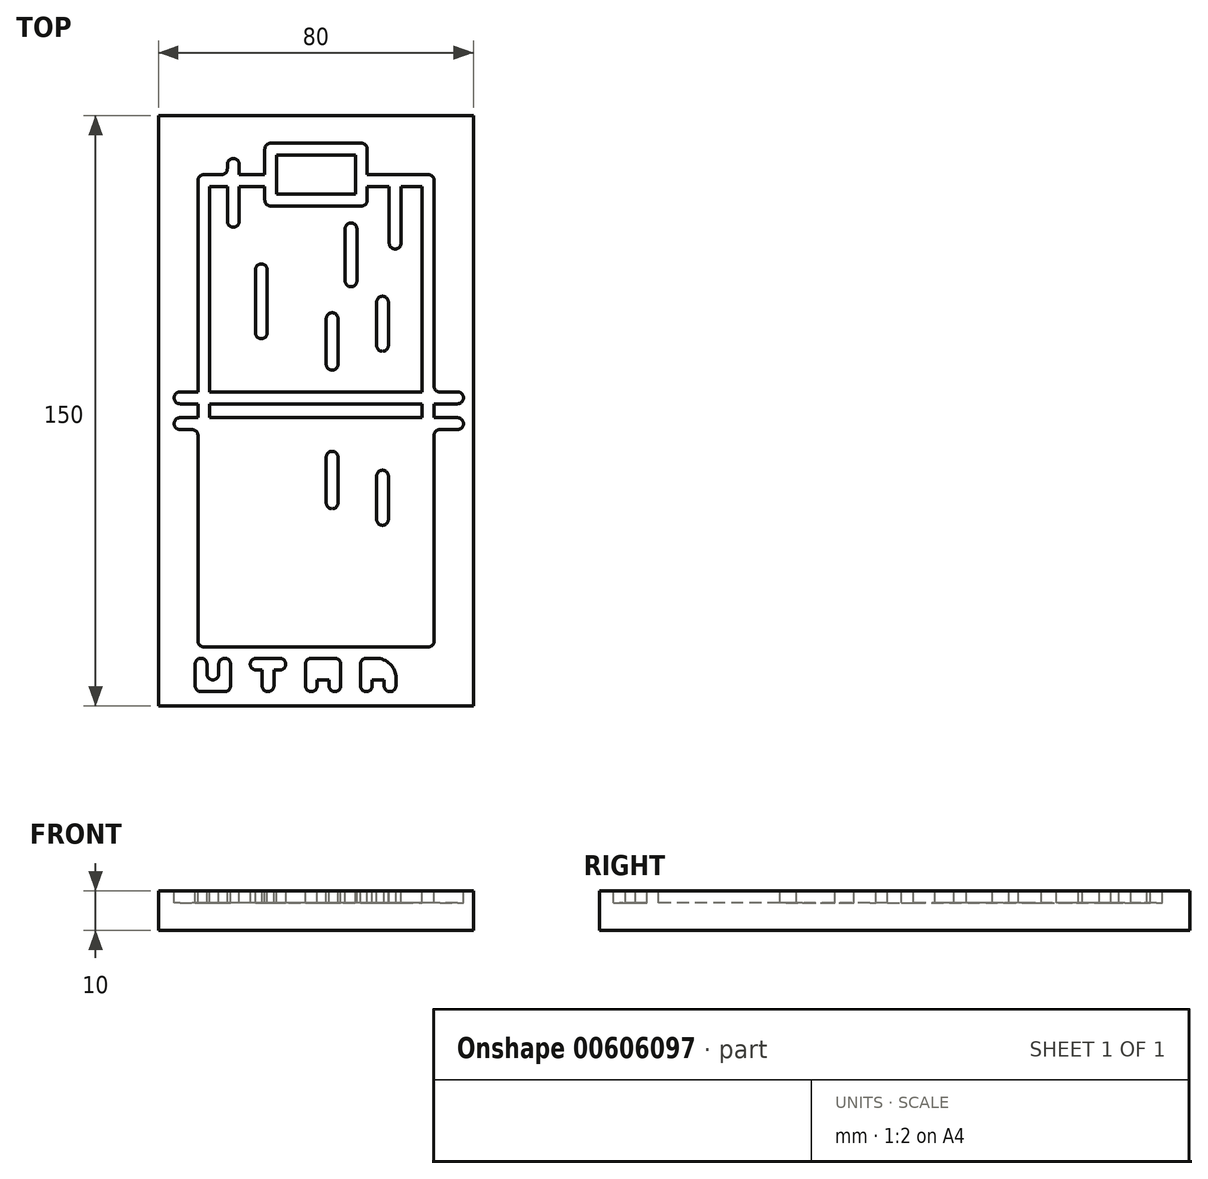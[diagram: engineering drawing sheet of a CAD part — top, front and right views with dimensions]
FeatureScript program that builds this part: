
annotation { "Feature Type Name" : "Feature", "Feature Type Description" : "" }
export const myFeature = defineFeature(function(context is Context, id is Id, definition is map)
    precondition{}
    {
        {
            var Q0;
            Q0=qCreatedBy(makeId("Top.planeOp"),FACE);
            var sketch = newSketch(context, id + "F0", { "sketchPlane" : qUnion([Q0])});
            skLineSegment(sketch, "E0.bottom", {"start": v(40, 75) * mm, "end": v(-40, 75) * mm});
            skLineSegment(sketch, "E0.top", {"start": v(40, -75) * mm, "end": v(-40, -75) * mm});
            skLineSegment(sketch, "E0.left", {"start": v(40, 75) * mm, "end": v(40, -75) * mm});
            skLineSegment(sketch, "E0.right", {"start": v(-40, 75) * mm, "end": v(-40, -75) * mm});
            skPoint(sketch, "E0.middle", {"position": v(0, 0) * mm});
            skSolve(sketch);
        }
        {
            var Q0;
            Q0 = qSketchRegion(id + "F0", true);
            extrude(context, id + "F1", {"entities" : qUnion([Q0]), "depth" : 10 * mm, "offsetDistance" : 25.4 * mm});
        }
        {
            var Q0;
            Q0=makeQuery(id+"F1.opExtrude","CAP_FACE",FACE,{"disambiguationData":[OSD([sQuery(id+"F0.wireOp",EDGE,"E0.bottom"),sQuery(id+"F0.wireOp",EDGE,"E0.top"),sQuery(id+"F0.wireOp",EDGE,"E0.left"),sQuery(id+"F0.wireOp",EDGE,"E0.right")])],"isStart":false});
            var sketch = newSketch(context, id + "F2", { "sketchPlane" : qUnion([Q0])});
            skLineSegment(sketch, "E1.bottom", {"start": v(30, 60) * mm, "end": v(13, 60) * mm});
            skLineSegment(sketch, "E1.top", {"start": v(30, -60) * mm, "end": v(-30, -60) * mm});
            skLineSegment(sketch, "E1.left", {"start": v(30, 60) * mm, "end": v(30, 4.77) * mm});
            skLineSegment(sketch, "E1.right", {"start": v(-30, 60) * mm, "end": v(-30, 4.77) * mm});
            skPoint(sketch, "E1.middle", {"position": v(0, 0) * mm});
            skLineSegment(sketch, "E2", {"start": v(-15.4, 35.8) * mm, "end": v(-15.4, 19.8) * mm});
            skLineSegment(sketch, "E3.bottom", {"start": v(10, 55) * mm, "end": v(-10, 55) * mm});
            skLineSegment(sketch, "E3.top", {"start": v(10, 65) * mm, "end": v(-10, 65) * mm});
            skLineSegment(sketch, "E3.left", {"start": v(10, 55) * mm, "end": v(10, 65) * mm});
            skLineSegment(sketch, "E3.right", {"start": v(-10, 55) * mm, "end": v(-10, 65) * mm});
            skPoint(sketch, "E3.middle", {"position": v(0, 60) * mm});
            skLineSegment(sketch, "E4", {"start": v(7.4, 46.2) * mm, "end": v(7.4, 33) * mm});
            skLineSegment(sketch, "E5", {"start": v(2.6, 23.4) * mm, "end": v(2.6, 11.8) * mm});
            skLineSegment(sketch, "E6", {"start": v(18.6, 57) * mm, "end": v(18.6, 42.6) * mm});
            skLineSegment(sketch, "E7", {"start": v(15.4, 27.6) * mm, "end": v(15.4, 16.6) * mm});
            skLineSegment(sketch, "E8", {"start": v(-34.55, 4.77) * mm, "end": v(-30, 4.77) * mm});
            skLineSegment(sketch, "E9", {"start": v(35.96, 1.77) * mm, "end": v(30, 1.77) * mm});
            skLineSegment(sketch, "E10", {"start": v(-30, -60) * mm, "end": v(-27, -60) * mm});
            skLineSegment(sketch, "E11", {"start": v(-27, -57) * mm, "end": v(-27, -4.77) * mm});
            skLineSegment(sketch, "E12", {"start": v(-30, 60) * mm, "end": v(-30, 57) * mm});
            skLineSegment(sketch, "E13", {"start": v(-27, 57) * mm, "end": v(-22.51, 57) * mm});
            skLineSegment(sketch, "E14", {"start": v(30, 60) * mm, "end": v(27, 60) * mm});
            skLineSegment(sketch, "E15", {"start": v(27, -57) * mm, "end": v(27, -4.77) * mm});
            skLineSegment(sketch, "E16", {"start": v(30, -60) * mm, "end": v(30, -57) * mm});
            skLineSegment(sketch, "E17", {"start": v(27, -57) * mm, "end": v(13.35, -57) * mm});
            skPoint(sketch, "E18.orphan", {"position": v(27, -60) * mm});
            skArc(sketch, "E19", {"start": v(-34.55, 1.77) * mm, "mid": v(-36.05, 3.27) * mm, "end": v(-34.55, 4.77) * mm});
            skArc(sketch, "E20", {"start": v(35.96, 1.77) * mm, "mid": v(37.46, 3.27) * mm, "end": v(35.96, 4.77) * mm});
            skArc(sketch, "E21.MirrorCS", {"start": v(35.96, -1.77) * mm, "mid": v(37.46, -3.27) * mm, "end": v(35.96, -4.77) * mm});
            skArc(sketch, "E22.MirrorCS", {"start": v(-34.55, -1.77) * mm, "mid": v(-36.05, -3.27) * mm, "end": v(-34.55, -4.77) * mm});
            skLineSegment(sketch, "E23.MirrorCS", {"start": v(35.96, -1.77) * mm, "end": v(30, -1.77) * mm});
            skLineSegment(sketch, "E24.MirrorCS", {"start": v(-34.55, -4.77) * mm, "end": v(-30, -4.77) * mm});
            skLineSegment(sketch, "E25", {"start": v(13, 65) * mm, "end": v(13, 60) * mm});
            skLineSegment(sketch, "E26", {"start": v(13, 52) * mm, "end": v(-13, 52) * mm});
            skLineSegment(sketch, "E27", {"start": v(-13, 52) * mm, "end": v(-13, 57) * mm});
            skLineSegment(sketch, "E28", {"start": v(-13, 68) * mm, "end": v(13, 68) * mm});
            skLineSegment(sketch, "E29", {"start": v(13, 68) * mm, "end": v(13, 65) * mm});
            skLineSegment(sketch, "E30.trimOffspring", {"start": v(-27, 4.77) * mm, "end": v(-27, 57) * mm});
            skLineSegment(sketch, "E31.trimOffspring", {"start": v(-27, 4.77) * mm, "end": v(27, 4.77) * mm});
            skLineSegment(sketch, "E32.trimOffspring", {"start": v(-30, 1.77) * mm, "end": v(-30, -1.77) * mm});
            skLineSegment(sketch, "E33.trimOffspring", {"start": v(-30, 1.77) * mm, "end": v(-34.55, 1.77) * mm});
            skLineSegment(sketch, "E34.trimOffspring", {"start": v(-30, -1.77) * mm, "end": v(-34.55, -1.77) * mm});
            skLineSegment(sketch, "E35.trimOffspring", {"start": v(-30, -4.77) * mm, "end": v(-30, -60) * mm});
            skLineSegment(sketch, "E36.trimOffspring", {"start": v(-27, -4.77) * mm, "end": v(27, -4.77) * mm});
            skLineSegment(sketch, "E37.trimOffspring", {"start": v(-27, -1.77) * mm, "end": v(-27, 1.77) * mm});
            skLineSegment(sketch, "E38.trimOffspring", {"start": v(27, -1.77) * mm, "end": v(27, 1.77) * mm});
            skLineSegment(sketch, "E39.trimOffspring", {"start": v(27, -1.77) * mm, "end": v(-27, -1.77) * mm});
            skLineSegment(sketch, "E40.trimOffspring", {"start": v(30, -4.77) * mm, "end": v(30, -60) * mm});
            skLineSegment(sketch, "E41.trimOffspring", {"start": v(30, -4.77) * mm, "end": v(35.96, -4.77) * mm});
            skLineSegment(sketch, "E42.trimOffspring", {"start": v(27, 1.77) * mm, "end": v(-27, 1.77) * mm});
            skLineSegment(sketch, "E43.trimOffspring", {"start": v(30, 4.77) * mm, "end": v(35.96, 4.77) * mm});
            skLineSegment(sketch, "E44.trimOffspring", {"start": v(27, 4.77) * mm, "end": v(27, 57) * mm});
            skLineSegment(sketch, "E45.trimOffspring", {"start": v(30, 1.77) * mm, "end": v(30, -1.77) * mm});
            skLineSegment(sketch, "E46", {"start": v(-19.51, 62.58) * mm, "end": v(-19.51, 60) * mm});
            skLineSegment(sketch, "E47", {"start": v(-22.51, 62.58) * mm, "end": v(-22.51, 60) * mm});
            skArc(sketch, "E48", {"start": v(-22.51, 48.15) * mm, "mid": v(-21.01, 46.65) * mm, "end": v(-19.51, 48.15) * mm});
            skArc(sketch, "E49", {"start": v(-22.51, 62.58) * mm, "mid": v(-21.01, 64.08) * mm, "end": v(-19.51, 62.58) * mm});
            skLineSegment(sketch, "E50.trimOffspring", {"start": v(-22.51, 57) * mm, "end": v(-22.51, 48.15) * mm});
            skLineSegment(sketch, "E51.trimOffspring", {"start": v(-22.51, 60) * mm, "end": v(-30, 60) * mm});
            skLineSegment(sketch, "E52.trimOffspring", {"start": v(-19.51, 57) * mm, "end": v(-13, 57) * mm});
            skLineSegment(sketch, "E53.trimOffspring", {"start": v(-19.51, 57) * mm, "end": v(-19.51, 48.15) * mm});
            skLineSegment(sketch, "E54", {"start": v(21.6, 42.6) * mm, "end": v(21.6, 57) * mm});
            skLineSegment(sketch, "E55.trimOffspring", {"start": v(21.6, 57) * mm, "end": v(27, 57) * mm});
            skArc(sketch, "E56", {"start": v(21.6, 42.6) * mm, "mid": v(20.1, 41.1) * mm, "end": v(18.6, 42.6) * mm});
            skLineSegment(sketch, "E57.trimOffspring", {"start": v(-13, 60) * mm, "end": v(-19.51, 60) * mm});
            skLineSegment(sketch, "E58.trimOffspring", {"start": v(13, 57) * mm, "end": v(18.6, 57) * mm});
            skLineSegment(sketch, "E59.trimOffspring", {"start": v(-13, 60) * mm, "end": v(-13, 68) * mm});
            skLineSegment(sketch, "E60.trimOffspring", {"start": v(13, 57) * mm, "end": v(13, 52) * mm});
            skLineSegment(sketch, "E61", {"start": v(-12.4, 35.8) * mm, "end": v(-12.4, 19.8) * mm});
            skArc(sketch, "E62", {"start": v(-12.4, 19.8) * mm, "mid": v(-13.9, 18.3) * mm, "end": v(-15.4, 19.8) * mm});
            skArc(sketch, "E63", {"start": v(-15.4, 35.8) * mm, "mid": v(-13.9, 37.3) * mm, "end": v(-12.4, 35.8) * mm});
            skLineSegment(sketch, "E64", {"start": v(10.4, 33) * mm, "end": v(10.4, 46.2) * mm});
            skArc(sketch, "E65", {"start": v(7.4, 46.2) * mm, "mid": v(8.9, 47.7) * mm, "end": v(10.4, 46.2) * mm});
            skArc(sketch, "E66", {"start": v(7.4, 33) * mm, "mid": v(8.9, 31.5) * mm, "end": v(10.4, 33) * mm});
            skLineSegment(sketch, "E67", {"start": v(5.6, 23.4) * mm, "end": v(5.6, 11.8) * mm});
            skArc(sketch, "E68", {"start": v(2.6, 11.8) * mm, "mid": v(4.1, 10.3) * mm, "end": v(5.6, 11.8) * mm});
            skArc(sketch, "E69", {"start": v(2.6, 23.4) * mm, "mid": v(4.1, 24.9) * mm, "end": v(5.6, 23.4) * mm});
            skLineSegment(sketch, "E70", {"start": v(18.4, 27.6) * mm, "end": v(18.4, 16.6) * mm});
            skArc(sketch, "E71", {"start": v(15.4, 16.6) * mm, "mid": v(16.9, 15.1) * mm, "end": v(18.4, 16.6) * mm});
            skArc(sketch, "E72", {"start": v(18.4, 27.6) * mm, "mid": v(16.9, 29.1) * mm, "end": v(15.4, 27.6) * mm});
            skArc(sketch, "E73.MirrorCS", {"start": v(15.4, -16.6) * mm, "mid": v(16.9, -15.1) * mm, "end": v(18.4, -16.6) * mm});
            skArc(sketch, "E74.MirrorCS", {"start": v(18.4, -27.6) * mm, "mid": v(16.9, -29.1) * mm, "end": v(15.4, -27.6) * mm});
            skArc(sketch, "E75.MirrorCS", {"start": v(2.6, -11.8) * mm, "mid": v(4.1, -10.3) * mm, "end": v(5.6, -11.8) * mm});
            skArc(sketch, "E76.MirrorCS", {"start": v(2.6, -23.4) * mm, "mid": v(4.1, -24.9) * mm, "end": v(5.6, -23.4) * mm});
            skLineSegment(sketch, "E77.MirrorCS", {"start": v(18.4, -27.6) * mm, "end": v(18.4, -16.6) * mm});
            skLineSegment(sketch, "E78.MirrorCS", {"start": v(15.4, -27.6) * mm, "end": v(15.4, -16.6) * mm});
            skLineSegment(sketch, "E79.MirrorCS", {"start": v(5.6, -23.4) * mm, "end": v(5.6, -11.8) * mm});
            skLineSegment(sketch, "E80.MirrorCS", {"start": v(2.6, -23.4) * mm, "end": v(2.6, -11.8) * mm});
            skArc(sketch, "E81.MirrorCS", {"start": v(-12.4, -19.8) * mm, "mid": v(-13.9, -18.3) * mm, "end": v(-15.4, -19.8) * mm});
            skLineSegment(sketch, "E82.MirrorCS", {"start": v(-15.4, -35.8) * mm, "end": v(-15.4, -19.8) * mm});
            skLineSegment(sketch, "E83.MirrorCS", {"start": v(-12.4, -35.8) * mm, "end": v(-12.4, -19.8) * mm});
            skArc(sketch, "E84.MirrorCS", {"start": v(-15.4, -35.8) * mm, "mid": v(-13.9, -37.3) * mm, "end": v(-12.4, -35.8) * mm});
            skLineSegment(sketch, "E85.top", {"start": v(13.35, -40.36) * mm, "end": v(-13.35, -40.36) * mm});
            skLineSegment(sketch, "E85.left", {"start": v(13.35, -57) * mm, "end": v(13.35, -40.36) * mm});
            skLineSegment(sketch, "E85.right", {"start": v(-13.35, -57) * mm, "end": v(-13.35, -40.36) * mm});
            skPoint(sketch, "E85.middle", {"position": v(0, -48.68) * mm});
            skLineSegment(sketch, "E86.trimOffspring", {"start": v(-13.35, -57) * mm, "end": v(-27, -57) * mm});
            skLineSegment(sketch, "E87", {"start": v(-30.7, -64.37) * mm, "end": v(-30.7, -71.37) * mm});
            skArc(sketch, "E88", {"start": v(-30.7, -64.37) * mm, "mid": v(-29.2, -62.87) * mm, "end": v(-27.7, -64.37) * mm});
            skLineSegment(sketch, "E89", {"start": v(-27.7, -64.37) * mm, "end": v(-27.7, -66.87) * mm});
            skLineSegment(sketch, "E90", {"start": v(-24.7, -66.87) * mm, "end": v(-24.7, -64.37) * mm});
            skLineSegment(sketch, "E91", {"start": v(-21.7, -64.37) * mm, "end": v(-21.7, -71.37) * mm});
            skLineSegment(sketch, "E92", {"start": v(-30.7, -71.37) * mm, "end": v(-21.7, -71.37) * mm});
            skArc(sketch, "E93", {"start": v(-21.7, -64.37) * mm, "mid": v(-23.2, -62.87) * mm, "end": v(-24.7, -64.37) * mm});
            skArc(sketch, "E94", {"start": v(-24.7, -66.87) * mm, "mid": v(-26.2, -68.37) * mm, "end": v(-27.7, -66.87) * mm});
            skLineSegment(sketch, "E95", {"start": v(-16.7, -62.87) * mm, "end": v(-7.7, -62.87) * mm});
            skLineSegment(sketch, "E96", {"start": v(-7.7, -62.87) * mm, "end": v(-7.7, -65.87) * mm});
            skLineSegment(sketch, "E97", {"start": v(-7.7, -65.87) * mm, "end": v(-10.7, -65.87) * mm});
            skLineSegment(sketch, "E98", {"start": v(-10.7, -65.87) * mm, "end": v(-10.7, -71.37) * mm});
            skLineSegment(sketch, "E99", {"start": v(-10.7, -71.37) * mm, "end": v(-13.7, -71.37) * mm});
            skLineSegment(sketch, "E100", {"start": v(-13.7, -71.37) * mm, "end": v(-13.7, -65.87) * mm});
            skLineSegment(sketch, "E101", {"start": v(-13.7, -65.87) * mm, "end": v(-16.7, -65.87) * mm});
            skLineSegment(sketch, "E102", {"start": v(-16.7, -65.87) * mm, "end": v(-16.7, -62.87) * mm});
            skLineSegment(sketch, "E103", {"start": v(-2.7, -62.87) * mm, "end": v(-2.7, -71.37) * mm});
            skLineSegment(sketch, "E104", {"start": v(-2.7, -71.37) * mm, "end": v(0.3, -71.37) * mm});
            skLineSegment(sketch, "E105", {"start": v(0.3, -71.37) * mm, "end": v(0.3, -68.37) * mm});
            skLineSegment(sketch, "E106", {"start": v(0.3, -68.37) * mm, "end": v(3.3, -68.37) * mm});
            skLineSegment(sketch, "E107", {"start": v(3.3, -68.37) * mm, "end": v(3.3, -71.37) * mm});
            skLineSegment(sketch, "E108", {"start": v(3.3, -71.37) * mm, "end": v(6.3, -71.37) * mm});
            skLineSegment(sketch, "E109", {"start": v(6.3, -71.37) * mm, "end": v(6.3, -62.87) * mm});
            skLineSegment(sketch, "E110", {"start": v(6.3, -62.87) * mm, "end": v(-2.7, -62.87) * mm});
            skLineSegment(sketch, "E111", {"start": v(6.3, -62.87) * mm, "end": v(11.3, -62.87) * mm});
            skLineSegment(sketch, "E112", {"start": v(11.3, -62.87) * mm, "end": v(11.3, -71.37) * mm});
            skLineSegment(sketch, "E113", {"start": v(11.3, -71.37) * mm, "end": v(14.3, -71.37) * mm});
            skLineSegment(sketch, "E114", {"start": v(14.3, -71.37) * mm, "end": v(14.3, -68.37) * mm});
            skLineSegment(sketch, "E115", {"start": v(14.3, -68.37) * mm, "end": v(17.3, -68.37) * mm});
            skLineSegment(sketch, "E116", {"start": v(17.3, -68.37) * mm, "end": v(17.3, -71.37) * mm});
            skLineSegment(sketch, "E117", {"start": v(17.3, -71.37) * mm, "end": v(20.3, -71.37) * mm});
            skLineSegment(sketch, "E118", {"start": v(20.3, -71.37) * mm, "end": v(20.3, -62.87) * mm});
            skLineSegment(sketch, "E119", {"start": v(20.3, -62.87) * mm, "end": v(11.3, -62.87) * mm});
            skSolve(sketch);
        }
        {
            var Q0;
            Q0 = qSketchRegion(id + "F2", true);
            var Q1;
            Q1=makeQuery(id+"F2.imprint","IMPRINT",FACE,{"disambiguationData":[TD([[makeQuery(id+"F2.imprint","IMPRINT",EDGE,{"derivedFrom":sQuery(id+"F2.wireOp",EDGE,"E2")}),1.0]])]});
            var Q2;
            Q2=makeQuery(id+"F2.imprint","IMPRINT",FACE,{"disambiguationData":[TD([[makeQuery(id+"F2.imprint","IMPRINT",EDGE,{"derivedFrom":sQuery(id+"F2.wireOp",EDGE,"E4")}),1.0]])]});
            var Q3;
            Q3=makeQuery(id+"F2.imprint","IMPRINT",FACE,{"disambiguationData":[TD([[makeQuery(id+"F2.imprint","IMPRINT",EDGE,{"derivedFrom":sQuery(id+"F2.wireOp",EDGE,"E5")}),1.0]])]});
            var Q4;
            Q4=makeQuery(id+"F2.imprint","IMPRINT",FACE,{"disambiguationData":[TD([[makeQuery(id+"F2.imprint","IMPRINT",EDGE,{"derivedFrom":sQuery(id+"F2.wireOp",EDGE,"E7")}),1.0]])]});
            var Q5;
            Q5=makeQuery(id+"F2.imprint","IMPRINT",FACE,{"disambiguationData":[TD([[makeQuery(id+"F2.imprint","IMPRINT",EDGE,{"derivedFrom":sQuery(id+"F2.wireOp",EDGE,"E81.MirrorCS")}),1.0]])]});
            var Q6;
            Q6=makeQuery(id+"F2.imprint","IMPRINT",FACE,{"disambiguationData":[TD([[makeQuery(id+"F2.imprint","IMPRINT",EDGE,{"derivedFrom":sQuery(id+"F2.wireOp",EDGE,"E75.MirrorCS")}),-1.0]])]});
            var Q7;
            Q7=makeQuery(id+"F2.imprint","IMPRINT",FACE,{"disambiguationData":[TD([[makeQuery(id+"F2.imprint","IMPRINT",EDGE,{"derivedFrom":sQuery(id+"F2.wireOp",EDGE,"E73.MirrorCS")}),-1.0]])]});
            extrude(context, id + "F3", {"entities" : qUnion([Q0, Q1, Q2, Q3, Q4, Q5, Q6, Q7]), "operationType" : NewBodyOperationType.REMOVE, "oppositeDirection" : true, "depth" : 3 * mm, "offsetDistance" : 25.4 * mm});
        }
        {
            var Q0;
            Q0=makeQuery(id+"F3.boolean.opBoolean","COPY",EDGE,{"derivedFrom":makeQuery(id+"F3.opExtrude","SWEPT_EDGE",EDGE,{"disambiguationData":[OSD([sQuery(id+"F2.wireOp",EDGE,"E26"),sQuery(id+"F2.wireOp",EDGE,"E27")])]})});
            var Q1;
            Q1=makeQuery(id+"F3.boolean.opBoolean","COPY",EDGE,{"derivedFrom":makeQuery(id+"F3.opExtrude","SWEPT_EDGE",EDGE,{"disambiguationData":[OSD([sQuery(id+"F2.wireOp",EDGE,"E28"),sQuery(id+"F2.wireOp",EDGE,"E59.trimOffspring")])]})});
            var Q2;
            Q2=makeQuery(id+"F3.boolean.opBoolean","COPY",EDGE,{"derivedFrom":makeQuery(id+"F3.opExtrude","SWEPT_EDGE",EDGE,{"disambiguationData":[OSD([sQuery(id+"F2.wireOp",EDGE,"E28"),sQuery(id+"F2.wireOp",EDGE,"E29")])]})});
            var Q3;
            Q3=makeQuery(id+"F3.boolean.opBoolean","COPY",EDGE,{"derivedFrom":makeQuery(id+"F3.opExtrude","SWEPT_EDGE",EDGE,{"disambiguationData":[OSD([sQuery(id+"F2.wireOp",EDGE,"E26"),sQuery(id+"F2.wireOp",EDGE,"E60.trimOffspring")])]})});
            var Q4;
            Q4=makeQuery(id+"F3.boolean.opBoolean","COPY",EDGE,{"derivedFrom":makeQuery(id+"F3.opExtrude","SWEPT_EDGE",EDGE,{"disambiguationData":[OSD([sQuery(id+"F2.wireOp",EDGE,"E1.top"),sQuery(id+"F2.wireOp",EDGE,"E40.trimOffspring")])]})});
            var Q5;
            Q5=makeQuery(id+"F3.boolean.opBoolean","COPY",EDGE,{"derivedFrom":makeQuery(id+"F3.opExtrude","SWEPT_EDGE",EDGE,{"disambiguationData":[OSD([sQuery(id+"F2.wireOp",EDGE,"E10"),sQuery(id+"F2.wireOp",EDGE,"E35.trimOffspring")])]})});
            var Q6;
            Q6=makeQuery(id+"F3.boolean.opBoolean","COPY",EDGE,{"derivedFrom":makeQuery(id+"F3.opExtrude","SWEPT_EDGE",EDGE,{"disambiguationData":[OSD([sQuery(id+"F2.wireOp",EDGE,"E85.top"),sQuery(id+"F2.wireOp",EDGE,"E85.right")])]})});
            var Q7;
            Q7=makeQuery(id+"F3.boolean.opBoolean","COPY",EDGE,{"derivedFrom":makeQuery(id+"F3.opExtrude","SWEPT_EDGE",EDGE,{"disambiguationData":[OSD([sQuery(id+"F2.wireOp",EDGE,"E85.top"),sQuery(id+"F2.wireOp",EDGE,"E85.left")])]})});
            var Q8;
            Q8=makeQuery(id+"F3.boolean.opBoolean","COPY",EDGE,{"derivedFrom":makeQuery(id+"F3.opExtrude","SWEPT_EDGE",EDGE,{"disambiguationData":[OSD([sQuery(id+"F2.wireOp",EDGE,"E87"),sQuery(id+"F2.wireOp",EDGE,"E92")])]})});
            var Q9;
            Q9=makeQuery(id+"F3.boolean.opBoolean","COPY",EDGE,{"derivedFrom":makeQuery(id+"F3.opExtrude","SWEPT_EDGE",EDGE,{"disambiguationData":[OSD([sQuery(id+"F2.wireOp",EDGE,"E91"),sQuery(id+"F2.wireOp",EDGE,"E92")])]})});
            var Q10;
            Q10=makeQuery(id+"F3.boolean.opBoolean","COPY",EDGE,{"derivedFrom":makeQuery(id+"F3.opExtrude","SWEPT_EDGE",EDGE,{"disambiguationData":[OSD([sQuery(id+"F2.wireOp",EDGE,"E98"),sQuery(id+"F2.wireOp",EDGE,"E99")])]})});
            var Q11;
            Q11=makeQuery(id+"F3.boolean.opBoolean","COPY",EDGE,{"derivedFrom":makeQuery(id+"F3.opExtrude","SWEPT_EDGE",EDGE,{"disambiguationData":[OSD([sQuery(id+"F2.wireOp",EDGE,"E96"),sQuery(id+"F2.wireOp",EDGE,"E97")])]})});
            var Q12;
            Q12=makeQuery(id+"F3.boolean.opBoolean","COPY",EDGE,{"derivedFrom":makeQuery(id+"F3.opExtrude","SWEPT_EDGE",EDGE,{"disambiguationData":[OSD([sQuery(id+"F2.wireOp",EDGE,"E99"),sQuery(id+"F2.wireOp",EDGE,"E100")])]})});
            var Q13;
            Q13=makeQuery(id+"F3.boolean.opBoolean","COPY",EDGE,{"derivedFrom":makeQuery(id+"F3.opExtrude","SWEPT_EDGE",EDGE,{"disambiguationData":[OSD([sQuery(id+"F2.wireOp",EDGE,"E101"),sQuery(id+"F2.wireOp",EDGE,"E102")])]})});
            var Q14;
            Q14=makeQuery(id+"F3.boolean.opBoolean","COPY",EDGE,{"derivedFrom":makeQuery(id+"F3.opExtrude","SWEPT_EDGE",EDGE,{"disambiguationData":[OSD([sQuery(id+"F2.wireOp",EDGE,"E95"),sQuery(id+"F2.wireOp",EDGE,"E102")])]})});
            var Q15;
            Q15=makeQuery(id+"F3.boolean.opBoolean","COPY",EDGE,{"derivedFrom":makeQuery(id+"F3.opExtrude","SWEPT_EDGE",EDGE,{"disambiguationData":[OSD([sQuery(id+"F2.wireOp",EDGE,"E95"),sQuery(id+"F2.wireOp",EDGE,"E96")])]})});
            var Q16;
            Q16=makeQuery(id+"F3.boolean.opBoolean","COPY",EDGE,{"derivedFrom":makeQuery(id+"F3.opExtrude","SWEPT_EDGE",EDGE,{"disambiguationData":[OSD([sQuery(id+"F2.wireOp",EDGE,"E109"),sQuery(id+"F2.wireOp",EDGE,"E110")])]})});
            var Q17;
            Q17=makeQuery(id+"F3.boolean.opBoolean","COPY",EDGE,{"derivedFrom":makeQuery(id+"F3.opExtrude","SWEPT_EDGE",EDGE,{"disambiguationData":[OSD([sQuery(id+"F2.wireOp",EDGE,"E103"),sQuery(id+"F2.wireOp",EDGE,"E110")])]})});
            var Q18;
            Q18=makeQuery(id+"F3.boolean.opBoolean","COPY",EDGE,{"derivedFrom":makeQuery(id+"F3.opExtrude","SWEPT_EDGE",EDGE,{"disambiguationData":[OSD([sQuery(id+"F2.wireOp",EDGE,"E112"),sQuery(id+"F2.wireOp",EDGE,"E119")])]})});
            var Q19;
            Q19=makeQuery(id+"F3.boolean.opBoolean","COPY",EDGE,{"derivedFrom":makeQuery(id+"F3.opExtrude","SWEPT_EDGE",EDGE,{"disambiguationData":[OSD([sQuery(id+"F2.wireOp",EDGE,"E117"),sQuery(id+"F2.wireOp",EDGE,"E118")])]})});
            var Q20;
            Q20=makeQuery(id+"F3.boolean.opBoolean","COPY",EDGE,{"derivedFrom":makeQuery(id+"F3.opExtrude","SWEPT_EDGE",EDGE,{"disambiguationData":[OSD([sQuery(id+"F2.wireOp",EDGE,"E113"),sQuery(id+"F2.wireOp",EDGE,"E114")])]})});
            var Q21;
            Q21=makeQuery(id+"F3.boolean.opBoolean","COPY",EDGE,{"derivedFrom":makeQuery(id+"F3.opExtrude","SWEPT_EDGE",EDGE,{"disambiguationData":[OSD([sQuery(id+"F2.wireOp",EDGE,"E108"),sQuery(id+"F2.wireOp",EDGE,"E109")])]})});
            var Q22;
            Q22=makeQuery(id+"F3.boolean.opBoolean","COPY",EDGE,{"derivedFrom":makeQuery(id+"F3.opExtrude","SWEPT_EDGE",EDGE,{"disambiguationData":[OSD([sQuery(id+"F2.wireOp",EDGE,"E104"),sQuery(id+"F2.wireOp",EDGE,"E105")])]})});
            var Q23;
            Q23=makeQuery(id+"F3.boolean.opBoolean","COPY",EDGE,{"derivedFrom":makeQuery(id+"F3.opExtrude","SWEPT_EDGE",EDGE,{"disambiguationData":[OSD([sQuery(id+"F2.wireOp",EDGE,"E116"),sQuery(id+"F2.wireOp",EDGE,"E117")])]})});
            var Q24;
            Q24=makeQuery(id+"F3.boolean.opBoolean","COPY",EDGE,{"derivedFrom":makeQuery(id+"F3.opExtrude","SWEPT_EDGE",EDGE,{"disambiguationData":[OSD([sQuery(id+"F2.wireOp",EDGE,"E112"),sQuery(id+"F2.wireOp",EDGE,"E113")])]})});
            var Q25;
            Q25=makeQuery(id+"F3.boolean.opBoolean","COPY",EDGE,{"derivedFrom":makeQuery(id+"F3.opExtrude","SWEPT_EDGE",EDGE,{"disambiguationData":[OSD([sQuery(id+"F2.wireOp",EDGE,"E103"),sQuery(id+"F2.wireOp",EDGE,"E104")])]})});
            var Q26;
            Q26=makeQuery(id+"F3.boolean.opBoolean","COPY",EDGE,{"derivedFrom":makeQuery(id+"F3.opExtrude","SWEPT_EDGE",EDGE,{"disambiguationData":[OSD([sQuery(id+"F2.wireOp",EDGE,"E107"),sQuery(id+"F2.wireOp",EDGE,"E108")])]})});
            var Q27;
            Q27=makeQuery(id+"F3.boolean.opBoolean","COPY",EDGE,{"derivedFrom":makeQuery(id+"F3.opExtrude","SWEPT_EDGE",EDGE,{"disambiguationData":[OSD([sQuery(id+"F2.wireOp",EDGE,"E12"),sQuery(id+"F2.wireOp",EDGE,"E51.trimOffspring")])]})});
            var Q28;
            Q28=makeQuery(id+"F3.boolean.opBoolean","COPY",EDGE,{"derivedFrom":makeQuery(id+"F3.opExtrude","SWEPT_EDGE",EDGE,{"disambiguationData":[OSD([sQuery(id+"F2.wireOp",EDGE,"E1.left"),sQuery(id+"F2.wireOp",EDGE,"E14")])]})});
            fillet(context, id + "F4", {"entities" : qUnion([Q0, Q1, Q2, Q3, Q4, Q5, Q6, Q7, Q8, Q9, Q10, Q11, Q12, Q13, Q14, Q15, Q16, Q17, Q18, Q19, Q20, Q21, Q22, Q23, Q24, Q25, Q26, Q27, Q28]), "radius" : 1.5 * mm, "tangentPropagation" : true, "allowEdgeOverflow" : false});
        }
        {
            var Q0;
            Q0=makeQuery(id+"F3.boolean.opBoolean","COPY",EDGE,{"derivedFrom":makeQuery(id+"F3.opExtrude","SWEPT_EDGE",EDGE,{"disambiguationData":[OSD([sQuery(id+"F2.wireOp",EDGE,"E118"),sQuery(id+"F2.wireOp",EDGE,"E119")])]})});
            fillet(context, id + "F5", {"entities" : qUnion([Q0]), "radius" : 5.08 * mm, "tangentPropagation" : true, "allowEdgeOverflow" : false});
        }
    });
